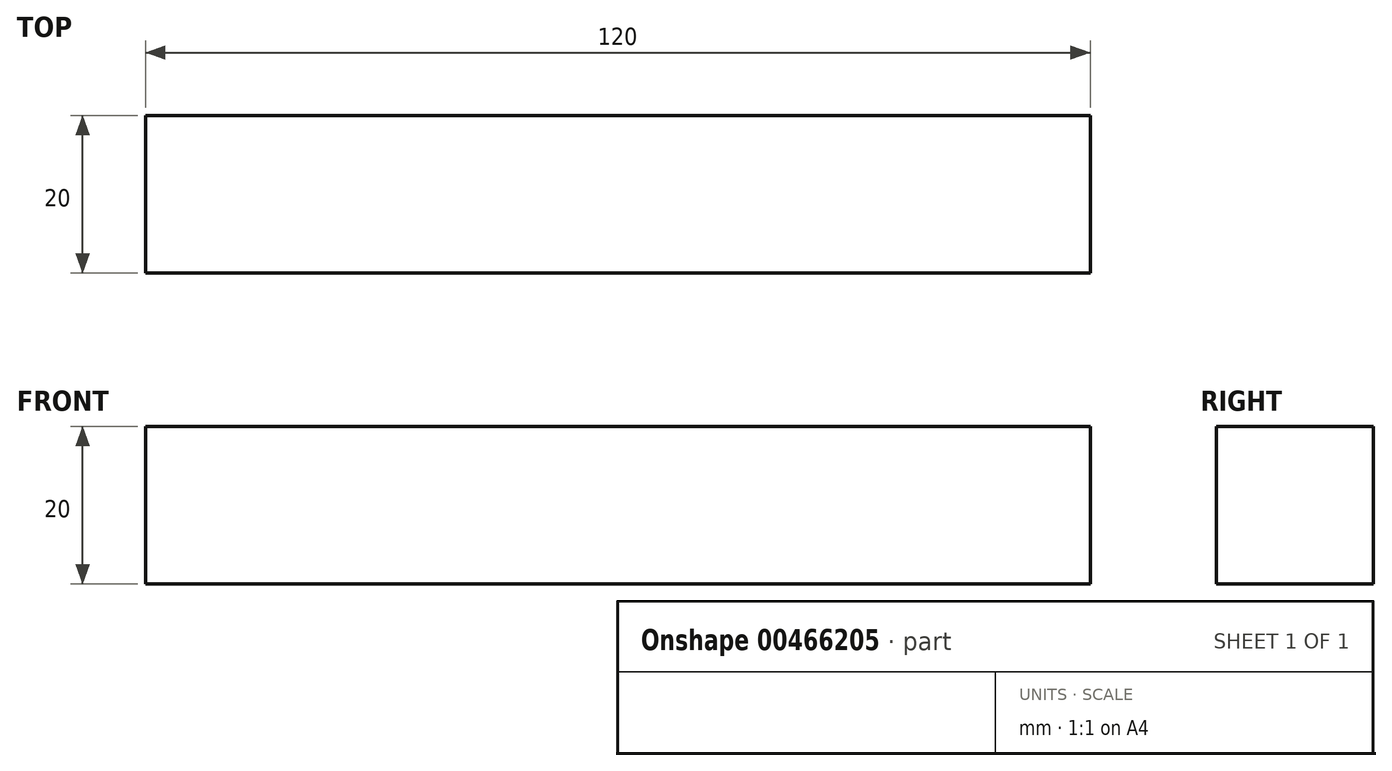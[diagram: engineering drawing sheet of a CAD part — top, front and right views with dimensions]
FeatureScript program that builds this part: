
annotation { "Feature Type Name" : "Feature", "Feature Type Description" : "" }
export const myFeature = defineFeature(function(context is Context, id is Id, definition is map)
    precondition{}
    {
        {
            var Q0;
            Q0=qCreatedBy(makeId("Front.planeOp"),FACE);
            var sketch = newSketch(context, id + "F0", { "sketchPlane" : qUnion([Q0])});
            skLineSegment(sketch, "E0", {"start": v(0, 20) * mm, "end": v(0, 0) * mm});
            skLineSegment(sketch, "E1", {"start": v(0, 0) * mm, "end": v(120, 0) * mm});
            skSolve(sketch);
        }
        {
            var Q0;
            Q0 = qSketchRegion(id + "F0", true);
            var Q1;
            Q1 = qConstructionFilter(qBodyType(qCreatedBy(id + "F0" ,EDGE), BodyType.WIRE), ConstructionObject.NO);
            extrude(context, id + "F1", {"entities" : qUnion([Q0]), "bodyType" : ToolBodyType.SURFACE, "surfaceEntities" : qUnion([Q1]), "oppositeDirection" : true, "depth" : 20 * mm});
        }
        {
            var Q0;
            Q0=makeQuery(id+"F1.opExtrude","SWEPT_FACE",FACE,{"disambiguationData":[OSD([sQuery(id+"F0.wireOp",EDGE,"E1")])]});
            var sketch = newSketch(context, id + "F2", { "sketchPlane" : qUnion([Q0])});
            skLineSegment(sketch, "E2.0", {"start": v(0, 0) * mm, "end": v(120, 0) * mm});
            skLineSegment(sketch, "E3.0", {"start": v(120, 20) * mm, "end": v(0, 20) * mm});
            skSolve(sketch);
        }
        {
            var Q0;
            Q0 = qSketchRegion(id + "F2", true);
            var Q1;
            Q1 = qConstructionFilter(qBodyType(qCreatedBy(id + "F2" ,EDGE), BodyType.WIRE), ConstructionObject.NO);
            extrude(context, id + "F3", {"entities" : qUnion([Q0]), "bodyType" : ToolBodyType.SURFACE, "surfaceEntities" : qUnion([Q1]), "depth" : 20 * mm});
        }
    });
